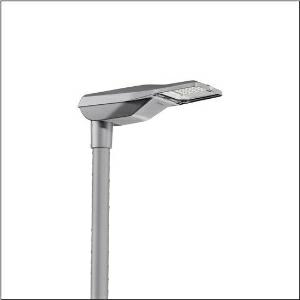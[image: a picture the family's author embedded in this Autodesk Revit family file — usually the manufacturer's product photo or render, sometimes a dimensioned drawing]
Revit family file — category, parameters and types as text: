
# Revit family: streetlight_sl_21_iq_micro___st0_8a_5xe1c61g08cb_671e
name_source: partatom
category: Lighting Fixtures
units: mm (PartAtom-declared; Revit-internal decimal feet)

## family parameters
Cut with Voids When Loaded = No
Host = Face
Light Source = No
Part Type = Normal
Room Calculation Point = No
Round Connector Dimension = Use Diameter
Shared = No

## types (1)
- --- (1 x LED, 2570 lm, 19.4 W, 2700K)
    Apparent Load = 19 VA
    CIE Flux Codes = 38 75 97 100 100
    Color Rendering = 70
    Color Temperature = 2700K
    Default Elevation = 1800 mm
    Description = Streetlight SL 21 iQ micro, mast luminaire, primary light control with lens, of PMMA, primary optical cover: cover, of toughened safety glass, transparent, light distribution: ST0.8a, light emission: direct distribution, primary light characteristic: asymmetric, installation type: post-top, side-entry, LED, High Power LED, rated luminous flux: 2.570lm, luminous efficacy: 133lm/W, light colour: 727, colour temperature: 2700K, control gear: iQ Street-Remote, control: Street-Remote, Auto-Match, Temp-Guard, Lumen-Switch, Night-Set, Smart-Wire, Light-Fading, Desk-Remote (wireless, voltage-free reading and setting of iQ features in the workshop via application-optimized NFC function/RFID function), optimised constant luminous flux control (CLO 2.0), pre-setting: linear dimming characteristic, mains connection: 220..240V, AC, 50/60Hz, start of lifetime: 19W, end of service life: 20W, reduction: 10W, luminaire housing, of diecast aluminium, powder-coated, Siteco® metallic grey (DB 702S), corrosivity category C5 mid according to DIN EN ISO 12944, please order mast flange separately, inclination adjustable: 0°, 5°, 10°, 15°, sealing non-destructively replaceable, multi-level sealing system, length: 528mm, width: 235mm, height: 110mm, mast flange for spigot size: 42mm (side-entry): 5XC10008XM4, 60/48mm (side-entry/post-top): 5XC10108XM2, 76/60mm (side-entry/post-top): 5XC10108XM1, protection rating (complete): IP66, insulation class (complete): insulation class II (safety insulation), certification: CE, ENEC, ENEC+, VDE, impact resistance: IK10, permissible operating ambient temperature for outdoor applications: -40..+50°C, standard-compliant lighting for roads and squares, packaging unit: 1 piece

Light Distribution: ST0.8a
    Height = 110 mm
    Lamp = 1 x LED
    Lamp Light Flux = 2570 lm
    Lamp Power = 19.4 W
    Lamp count = 1
    Length = 528 mm
    Luminous efficacy = 132 lm/W
    Manufacturer = Siteco
    ModVariant = No
    Model = 5XE1C61G08CB
    Number of Poles = 1
    OnlyDefault = Yes
    Power Factor = 1
    Product Name = Streetlight SL 21 iQ micro | ST0.8a
    Product group = mast luminaire | pylon top
    ProductGroupID = 6100
    Protection Class = Protection class II
    Protection Degree = IP 66
    RLX_Detail_Level = 1
    RLX_Emergency_Light_Flux = 0 lm
    RLX_Emergency_Type = 0
    RLX_Emergency_Type_DB = No
    RlxData = <blob elided: 99265 chars, md5=0a261d6d>
    Socket = socket
    Standby Power = 0 W
    System Light Flux = 2570 lm
    System Power = 19 W
    Type Comments = factory setting: luminous flux: 100 % | dim-lin: 254 | 387 mA
    Type Image = l_1006881.jpg
    URL = http://relux.com
    VarID = @adj_138284
    Voltage = 0 V
    Weight = 0.00 kg
    Width = 235 mm

## geometry (parser evidence)
native form markers: Blend x4, Sweep x11
no freeform markers — native parametric forms only
